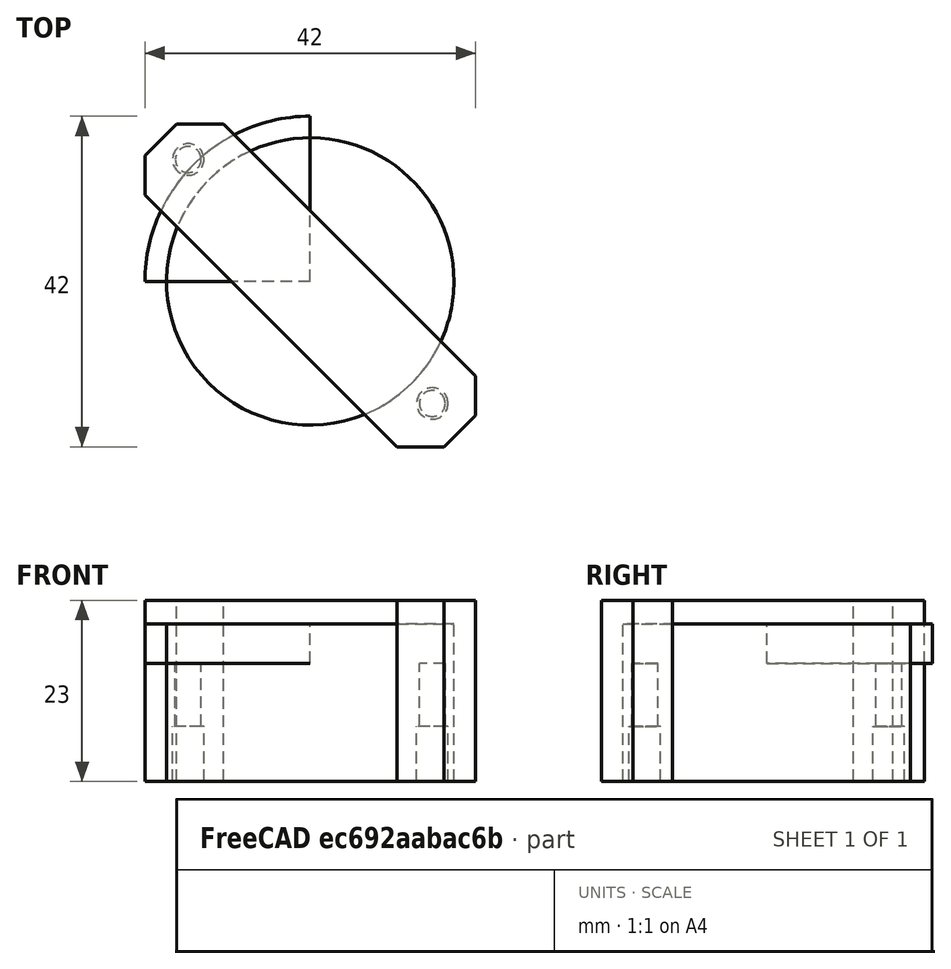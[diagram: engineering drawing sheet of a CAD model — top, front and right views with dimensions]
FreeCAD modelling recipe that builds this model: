
FCSTD DOCUMENT  (FreeCAD 0.18R16146 (Git))
Label: nema14-adapter
License: All rights reserved
LicenseURL: http://en.wikipedia.org/wiki/All_rights_reserved
objects: Part::Cylinder×6, Part::Chamfer×2, Part::Box×1, Part::MultiFuse×1
note: 10 computed .brp shape members not serialized (recipe doc carries the construction recipe); baked Part::Feature solids carry a one-line shape summary decoded from their .brp

FEATURE [Part::Box] Box  label="Cube"
  AttacherType = Attacher::AttachEngine3D
  Height = 23
  Length = 42
  Placement = pos=(-21,-21,0) rot=(0,0,1;0rad)
  Width = 41
FEATURE [Part::Cylinder] Cylinder
  Angle = 360
  AttacherType = Attacher::AttachEngine3D
  Height = 7
  Placement = pos=(15.5,-15.5,0) rot=(0,0,1;0rad)
  Radius = 2
FEATURE [Part::Cylinder] Cylinder002
  Angle = 360
  AttacherType = Attacher::AttachEngine3D
  Height = 7
  Placement = pos=(-15.5,15.5,0) rot=(0,0,1;0rad)
  Radius = 2
FEATURE [Part::Cylinder] Cylinder003
  Angle = 360
  AttacherType = Attacher::AttachEngine3D
  Height = 20
  Radius = 18.25
FEATURE [Part::Cylinder] Cylinder004
  Angle = 360
  AttacherType = Attacher::AttachEngine3D
  Height = 15
  Placement = pos=(-15.5,15.5,0) rot=(0,0,1;0rad)
  Radius = 1.65
FEATURE [Part::Cylinder] Cylinder005
  Angle = 360
  AttacherType = Attacher::AttachEngine3D
  Height = 15
  Placement = pos=(15.5,-15.5,0) rot=(0,0,1;0rad)
  Radius = 1.65
FEATURE [Part::MultiFuse] Fusion
  Shapes = -> [Cylinder004,Cylinder005,Cylinder003,Cylinder002,Cylinder]
FEATURE [Part::Chamfer] Chamfer
  Base = -> Box
  Edges = 2 edges r=4: [Edge3,Edge5]
FEATURE [Part::Chamfer] Chamfer001
  Base = -> Chamfer
  Edges = 2 edges r=32: [Edge3,Edge17]
FEATURE [Part::Cylinder] Cylinder006
  Angle = 90
  AttacherType = Attacher::AttachEngine3D
  Height = 5
  Placement = pos=(0,0,15) rot=(0,0,1;1.5708rad)
  Radius = 21
